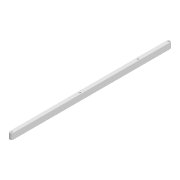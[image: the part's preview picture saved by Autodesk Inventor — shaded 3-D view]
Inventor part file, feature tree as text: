
AUTODESK INVENTOR PART (.ipt)
format: ipt  version: 2022 (Build 260153000, 153)  size: 93,696 bytes
history: native  units: mm
features: extrude x1, sketch x1
ambient origin geometry x8: Origin, YZ Plane, XZ Plane, XY Plane, X Axis, Y Axis, Z Axis, Center Point
bodies: Solid1 (feature_tree)
feature tree (2):
  extrude  "Extrusion1"  Depth=270.517mm
  sketch  "Sketch1"  dims[d0=6.0mm d1=270.517mm d2=3.0mm d3=3.0mm d4=10.0mm d5=0.0mm d10=3.0mm d11=117.696mm d12=3.0mm d13=217.699mm]
